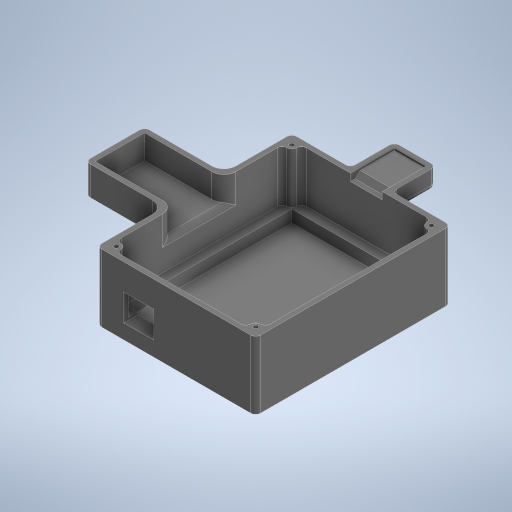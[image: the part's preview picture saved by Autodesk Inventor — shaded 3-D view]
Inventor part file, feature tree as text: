
AUTODESK INVENTOR PART (.ipt)
format: ipt  version: 2023 (Build 270158000, 158)  size: 526,336 bytes
history: native  units: mm
features: extrude x14, sketch x14, fillet x8, other x1, chamfer x1
ambient origin geometry x8: Origin, YZ Plane, XZ Plane, XY Plane, X Axis, Y Axis, Z Axis, Center Point
bodies: Body1 (feature_tree)
feature tree (38):
  other  "Sólido1"
  extrude  "Extrusão1"  Depth=80.8mm
  extrude  "Extrusão2"  Depth=2.0mm
  extrude  "Extrusão3"  Depth=2.0mm
  extrude  "Extrusão4"  Depth=21.0mm TaperAngle=0.0deg
  extrude  "Extrusão5"  Depth=1.9mm
  extrude  "Extrusão6"  Depth=2.0mm
  extrude  "Extrusão7"  Depth=1.9mm
  extrude  "Extrusão8"  Depth=7.0mm
  fillet  "Arredondamento1"  Radius=11.2mm
  extrude  "Extrusão10"  Depth=11.0mm
  extrude  "Extrusão11"  Depth=80.8mm
  fillet  "Arredondamento2"  Radius=12.0mm
  fillet  "Arredondamento3"  [1 undecoded]
  fillet  "Arredondamento4"  Radius=80.8mm
  fillet  "Arredondamento5"  Radius=28.15mm
  fillet  "Arredondamento6"  Radius=32.9mm
  fillet  "Arredondamento7"  Radius=24.5mm
  extrude  "Extrusão12"  Depth=10.0mm TaperAngle=0.0deg
  extrude  "Extrusão13"  Depth=2.0mm
  extrude  "Extrusão14"  Depth=8.0mm
  extrude  "Extrusão15"  Depth=4.0mm
  fillet  "Arredondamento8"  Radius=48.5mm
  chamfer  "Chanfro1"  Distance=80.8mm
  sketch  "Esboço1"  dims[d0=80.8mm d1=65.8mm]
  sketch  "Esboço3"  dims[d2=2.0mm d3=0.0mm d5=6.0mm]
  sketch  "Esboço4"  dims[d6=5.0mm d7=0.0mm d8=2.0mm]
  sketch  "Esboço5"  dims[d9=21.0mm d10=0.0mm d11=21.0mm d12=0.0mm]
  sketch  "Esboço6"  dims[d13=1.9mm d16=1.9mm]
  sketch  "Esboço7"  dims[d17=2.0mm d18=2.0mm]
  sketch  "Esboço8"  dims[d19=1.9mm d22=1.9mm]
  sketch  "Esboço9"  dims[d26=7.0mm d27=0.0mm d28=12.5mm d29=11.2mm]
  sketch  "Esboço11"  dims[d30=6.0mm d31=11.0mm]
  sketch  "Esboço12"  dims[d32=6.0mm d33=0.0mm d34=24.5mm d35=12.0mm d36=0.0mm d37=80.8mm d38=28.15mm d39=32.9mm d40=0.0mm d41=24.5mm]
  sketch  "Esboço13"  dims[d42=2.0mm d43=10.0mm d44=0.0mm]
  sketch  "Esboço14"  dims[d50=2.0mm d51=38.0mm]
  sketch  "Esboço15"  dims[d52=8.0mm d53=8.0mm]
  sketch  "Esboço16"  dims[d54=4.0mm d55=4.0mm d56=48.5mm d57=80.8mm d58=56.5mm d59=12.15mm d60=12.0mm d61=0.0mm d62=5.2mm d63=5.2mm d64=4.0mm d65=4.0mm d66=4.0mm d67=4.0mm d68=98.7mm d69=0.0mm d70=2.0mm d71=4.0mm d72=4.0mm d73=4.0mm d74=4.0mm d75=4.0mm d76=4.0mm d77=5.0mm d78=5.0mm d79=5.0mm d80=2.0mm d81=2.0mm d82=17.2mm d83=18.2mm d84=3.0mm d85=0.0mm d86=13.2mm d87=16.2mm d88=2.0mm d89=1.0mm d90=0.0mm d91=13.2mm d92=3.0mm d93=0.0mm d94=65.8mm d95=24.3mm d96=17.2mm d97=18.2mm d98=5.0mm d99=0.0mm d100=2.0mm d101=2.0mm d102=2.0mm d103=45.0deg]
note: 1 required parameter value undecoded (feature->parameter linkage not recoverable at this tier; creation-order binding heuristic only, values carry confidence <= 0.55)
